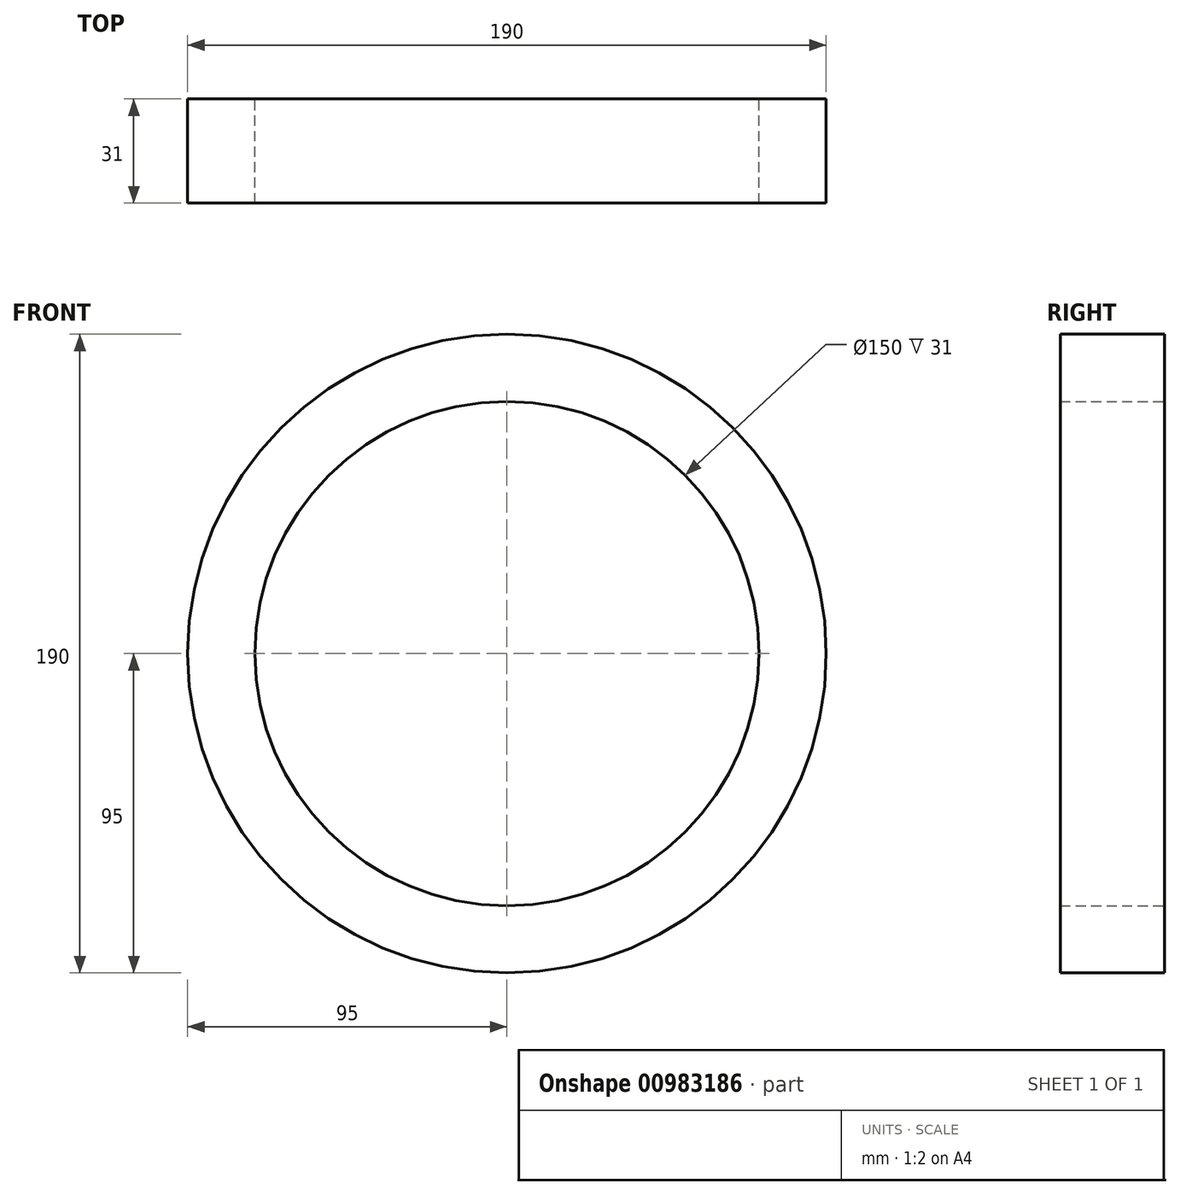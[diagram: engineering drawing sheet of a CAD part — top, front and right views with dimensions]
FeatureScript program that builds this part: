
annotation { "Feature Type Name" : "Feature", "Feature Type Description" : "" }
export const myFeature = defineFeature(function(context is Context, id is Id, definition is map)
    precondition{}
    {
        {
            var Q0;
            Q0=qCreatedBy(makeId("Front.planeOp"),FACE);
            var sketch = newSketch(context, id + "F0", { "sketchPlane" : qUnion([Q0])});
            skCircle(sketch, "E0", {"center": v(0, 0) * mm, "radius": 95 * mm});
            skCircle(sketch, "E1", {"center": v(0, 0) * mm, "radius": 75 * mm});
            skSolve(sketch);
        }
        {
            var Q0;
            Q0=makeQuery(id+"F0.imprint","IMPRINT",FACE,{"disambiguationData":[TD([[makeQuery(id+"F0.imprint","IMPRINT",EDGE,{"derivedFrom":sQuery(id+"F0.wireOp",EDGE,"E0")}),1.0]])]});
            extrude(context, id + "F1", {"entities" : qUnion([Q0]), "depth" : 31 * mm, "offsetDistance" : 25 * mm});
        }
    });
